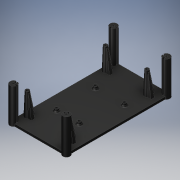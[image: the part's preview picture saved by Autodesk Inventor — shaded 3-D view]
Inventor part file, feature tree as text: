
AUTODESK INVENTOR PART (.ipt)
format: ipt  version: 2017 (Build 210142000, 142)  size: 301,056 bytes
history: native  units: in
note: dims shown in document units (in); Inventor stores cm internally (conversion verified against a paired STEP export)
features: reference x8, other x7, sketch x7, extrude x4
ambient origin geometry x8: Origin, YZ Plane, XZ Plane, XY Plane, X Axis, Y Axis, Z Axis, Center Point
bodies: Solid1 (feature_tree)
feature tree (26):
  extrude  "Extrusion1"  Depth=5.5in
  extrude  "Extrusion2"  Depth=0.375in
  extrude  "Extrusion3"  Depth=0.0938in
  other  "Boss4"
  extrude  "Extrusion4"  Depth=0.375in
  other  "Boss5"
  other  "Boss6"
  sketch  "Sketch1"  dims[d0=3.0in d1=5.5in]
  sketch  "Sketch2"  dims[d2=0.125in d3=0.0in d4=0.375in]
  sketch  "Sketch3"  dims[d5=0.0988in d6=0.0938in]
  sketch  "Sketch7"  dims[d7=0.375in d8=0.375in]
  sketch  "Sketch8"  dims[d9=0.375in]
  reference  "Reference2"
  reference  "Reference3"
  reference  "Reference4"
  reference  "Reference5"
  sketch  "Sketch9"  dims[d10=0.0938in]
  reference  "Reference6"
  reference  "Reference7"
  sketch  "Sketch10"  dims[d11=0.0938in d12=0.0938in d13=0.0938in d14=0.0938in d15=0.0938in d16=1.85in d17=0.0in d22=0.115in d23=0.115in d30=0.115in d31=0.115in d32=0.115in d39=0.115in d40=0.115in d41=0.115in d42=1.725in d43=0.0in d227=2.325in d229=1.568in d230=0.125in d231=0.125in d232=0.125in d233=0.125in d234=0.13in d235=0.13in d236=0.13in d237=0.465in d238=0.13in d239=0.13in d240=0.13in d241=0.13in d242=0.0635in d243=0.15in d244=0.2in d245=0.12in d246=0.38in d247=0.0137in d248=0.0069in d249=0.7874in d251=0.08in d252=0.08in d253=0.1in d254=0.0in d255=0.0687in d256=0.0172in d257=0.0in d258=0.0in d259=0.0in d260=90.0deg d261=0.005in d262=0.005in d263=0.005in d264=0.005in d265=0.375in d266=0.0in d267=0.0in d268=1.2in d269=0.2in d270=0.12in d271=0.38in d272=0.0137in d273=0.0069in d274=0.7874in d276=0.08in d277=0.08in d278=0.1in d279=0.0in d280=0.0687in d281=0.0172in d282=0.0in d283=0.0in d284=0.0in d285=90.0deg d286=0.0in d287=1.2in d288=0.2in d289=0.12in d290=0.38in d291=0.0137in d292=0.0069in d293=0.7874in d295=0.08in d296=0.08in d297=0.1in d298=0.0in d299=0.0687in d300=0.0172in d301=0.0in d302=0.0in d303=0.0in d304=90.0deg d305=1.8in d306=0.552in]
  reference  "Reference8"
  reference  "Reference9"
  parser-record x1  (decoder bookkeeping rows leaked as tree rows — omitted from the tree; the rows remain in map.json)
  other  "main_assy.iam"
  other  "Case Top:1"
  other  "PCB:1"
note: 1 file-system path scrubbed to <path> (originals preserved in map.json)
